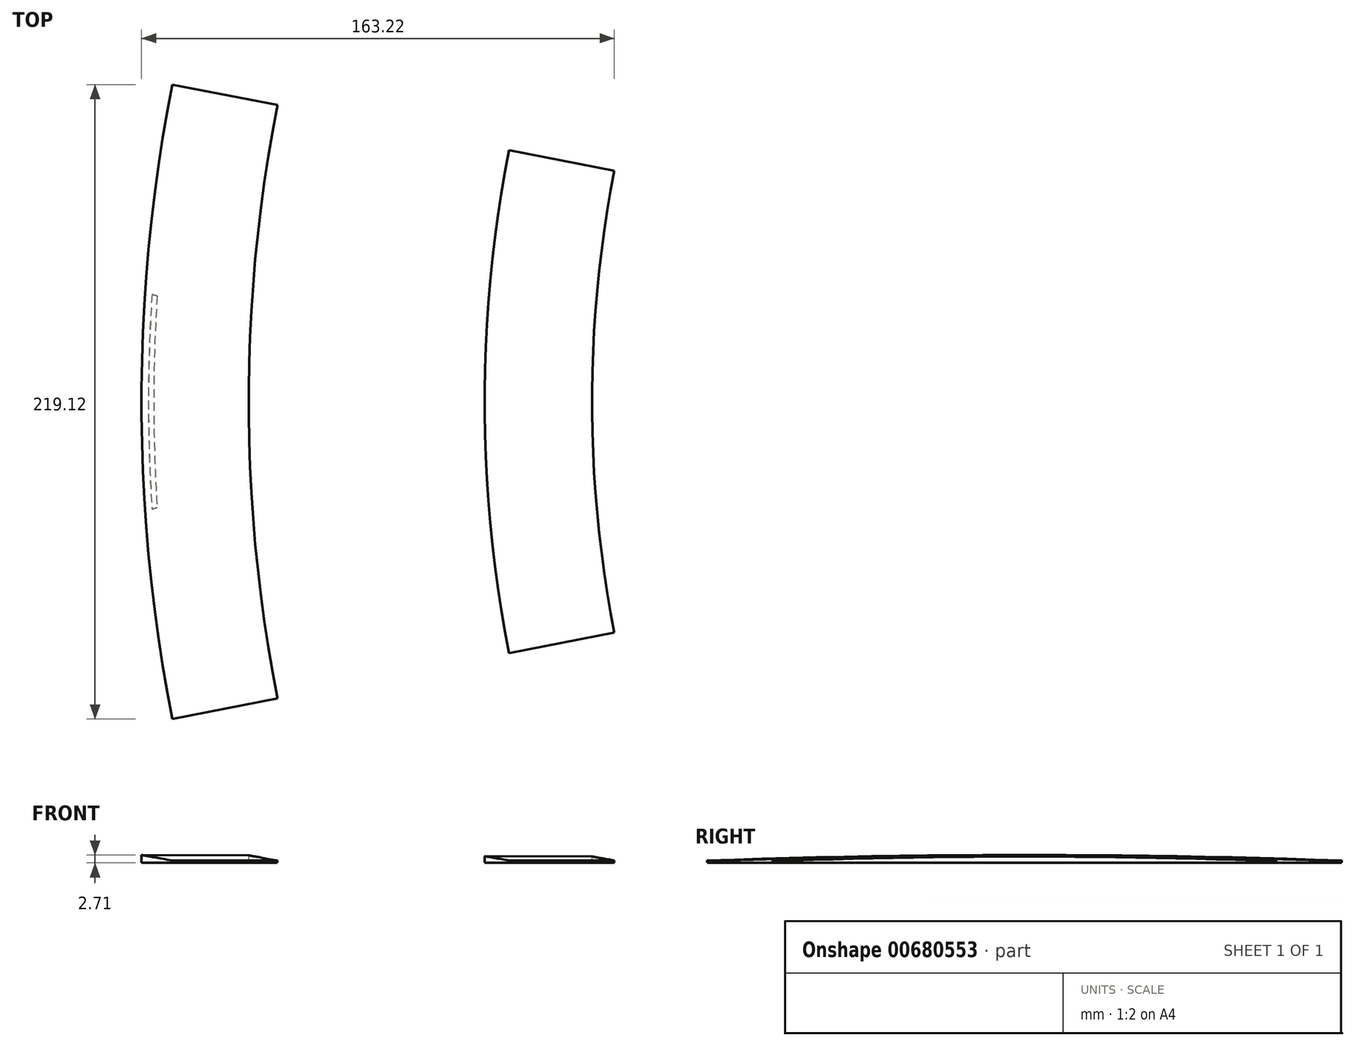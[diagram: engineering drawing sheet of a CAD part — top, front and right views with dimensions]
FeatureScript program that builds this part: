
annotation { "Feature Type Name" : "Feature", "Feature Type Description" : "" }
export const myFeature = defineFeature(function(context is Context, id is Id, definition is map)
    precondition{}
    {
        {
            var Q0;
            Q0=qCreatedBy(makeId("Front.planeOp"),FACE);
            var sketch = newSketch(context, id + "F0", { "sketchPlane" : qUnion([Q0])});
            skLineSegment(sketch, "E0", {"start": v(0, 1.91) * mm, "end": v(570.67, 0) * mm});
            skLineSegment(sketch, "E1", {"start": v(570.67, 0) * mm, "end": v(553.13, -97.53) * mm});
            skLineSegment(sketch, "E2", {"start": v(553.13, -97.53) * mm, "end": v(0, 1.91) * mm});
            skLineSegment(sketch, "E3", {"start": v(0, 1.91) * mm, "end": v(0.03, 9.71) * mm});
            skLineSegment(sketch, "E4", {"start": v(0.03, 9.71) * mm, "end": v(156.03, 9.19) * mm});
            skLineSegment(sketch, "E5", {"start": v(156.03, 9.19) * mm, "end": v(156, 1.39) * mm});
            skLineSegment(sketch, "E6", {"start": v(156, 1.39) * mm, "end": v(155.97, -7.61) * mm});
            skLineSegment(sketch, "E7", {"start": v(155.97, -7.61) * mm, "end": v(-0.03, -7.09) * mm});
            skLineSegment(sketch, "E8", {"start": v(-0.03, -7.09) * mm, "end": v(0, 1.91) * mm});
            skLineSegment(sketch, "E9", {"start": v(0.28, 9.71) * mm, "end": v(0.25, 1.91) * mm});
            skLineSegment(sketch, "E10", {"start": v(155.78, 9.2) * mm, "end": v(155.75, 1.4) * mm});
            skSolve(sketch);
        }
        {
            var Q0;
            {var subQ0=sQuery(id+"F0.wireOp",EDGE,"E9");Q0=makeQuery(id+"F0.imprint","IMPRINT",FACE,{"disambiguationData":[TD([[makeQuery(id+"F0.imprint","IMPRINT",EDGE,{"derivedFrom":subQ0}),1.0]])]});}
            var Q1;
            Q1=sQuery(id+"F0.wireOp",EDGE,"E1");
            revolve(context, id + "F1", {"entities" : qUnion([Q0]), "axis" : qUnion([Q1]), "revolveType" : RevolveType.SYMMETRIC, "angle" : 22.44 * degree});
        }
        {
            var Q0;
            Q0=qCreatedBy(makeId("Front.planeOp"),FACE);
            var sketch = newSketch(context, id + "F2", { "sketchPlane" : qUnion([Q0])});
            skLineSegment(sketch, "E11.bottom", {"start": v(-24.5, 7) * mm, "end": v(187.03, 7) * mm});
            skLineSegment(sketch, "E11.top", {"start": v(-24.5, -14.67) * mm, "end": v(187.03, -14.67) * mm});
            skLineSegment(sketch, "E11.left", {"start": v(-24.5, 7) * mm, "end": v(-24.5, -14.67) * mm});
            skLineSegment(sketch, "E11.right", {"start": v(187.03, 7) * mm, "end": v(187.03, -14.67) * mm});
            skSolve(sketch);
        }
        {
            var Q0;
            Q0=makeQuery(id+"F2.imprint","IMPRINT",FACE,{"disambiguationData":[TD([[makeQuery(id+"F2.imprint","IMPRINT",EDGE,{"derivedFrom":sQuery(id+"F2.wireOp",EDGE,"E11.bottom")}),-1.0]])]});
            extrude(context, id + "F3", {"entities" : qUnion([Q0]), "operationType" : NewBodyOperationType.REMOVE, "endBound" : BoundingType.SYMMETRIC, "depth" : 272.4 * mm, "offsetDistance" : 25 * mm});
        }
        {
            var Q0;
            Q0=qCreatedBy(makeId("Front.planeOp"),FACE);
            var sketch = newSketch(context, id + "F4", { "sketchPlane" : qUnion([Q0])});
            skLineSegment(sketch, "E12", {"start": v(0, 1.91) * mm, "end": v(570.67, 0) * mm});
            skLineSegment(sketch, "E13", {"start": v(570.67, 0) * mm, "end": v(553.13, -97.53) * mm});
            skLineSegment(sketch, "E14", {"start": v(553.13, -97.53) * mm, "end": v(0, 1.91) * mm});
            skLineSegment(sketch, "E15", {"start": v(0, 1.91) * mm, "end": v(0, 2.71) * mm});
            skLineSegment(sketch, "E16", {"start": v(0, 2.71) * mm, "end": v(1.7, 2.71) * mm});
            skLineSegment(sketch, "E17", {"start": v(1.7, 2.71) * mm, "end": v(2.7, 7.22) * mm});
            skLineSegment(sketch, "E18", {"start": v(2.7, 7.22) * mm, "end": v(4.5, 7.21) * mm});
            skLineSegment(sketch, "E19", {"start": v(4.5, 7.21) * mm, "end": v(4.49, 2.71) * mm});
            skLineSegment(sketch, "E20", {"start": v(4.49, 2.71) * mm, "end": v(1.7, 2.71) * mm});
            skLineSegment(sketch, "E21", {"start": v(156, 1.39) * mm, "end": v(156, 2.19) * mm});
            skLineSegment(sketch, "E22", {"start": v(156, 2.19) * mm, "end": v(154.3, 2.19) * mm});
            skLineSegment(sketch, "E23", {"start": v(154.3, 2.19) * mm, "end": v(153.3, 6.69) * mm});
            skLineSegment(sketch, "E24", {"start": v(153.3, 6.69) * mm, "end": v(151.5, 6.7) * mm});
            skLineSegment(sketch, "E25", {"start": v(151.5, 6.7) * mm, "end": v(151.49, 2.19) * mm});
            skLineSegment(sketch, "E26", {"start": v(151.49, 2.19) * mm, "end": v(154.3, 2.19) * mm});
            skLineSegment(sketch, "E27", {"start": v(37.29, 15.7) * mm, "end": v(37.25, 4.66) * mm});
            skLineSegment(sketch, "E28", {"start": v(37.25, 4.66) * mm, "end": v(40.75, 4.66) * mm});
            skLineSegment(sketch, "E29", {"start": v(40.75, 4.66) * mm, "end": v(40.8, 17.47) * mm});
            skLineSegment(sketch, "E30", {"start": v(40.8, 17.47) * mm, "end": v(37.29, 15.7) * mm});
            skLineSegment(sketch, "E31", {"start": v(115.3, 19.83) * mm, "end": v(115.25, 3.55) * mm});
            skLineSegment(sketch, "E32", {"start": v(115.25, 3.55) * mm, "end": v(118.75, 3.4) * mm});
            skLineSegment(sketch, "E33", {"start": v(118.75, 3.4) * mm, "end": v(118.8, 20.02) * mm});
            skLineSegment(sketch, "E34", {"start": v(118.8, 20.02) * mm, "end": v(115.3, 19.83) * mm});
            skLineSegment(sketch, "E35", {"start": v(40.8, 17.47) * mm, "end": v(115.3, 19.83) * mm});
            skLineSegment(sketch, "E36", {"start": v(40.75, 4.66) * mm, "end": v(115.25, 3.55) * mm});
            skSolve(sketch);
        }
        {
            var Q0;
            Q0=makeQuery(id+"F4.imprint","IMPRINT",FACE,{"disambiguationData":[TD([[makeQuery(id+"F4.imprint","IMPRINT",EDGE,{"derivedFrom":sQuery(id+"F4.wireOp",EDGE,"E17")}),-1.0]])]});
            var Q1;
            Q1=makeQuery(id+"F4.imprint","IMPRINT",FACE,{"disambiguationData":[TD([[makeQuery(id+"F4.imprint","IMPRINT",EDGE,{"derivedFrom":sQuery(id+"F4.wireOp",EDGE,"E23")}),1.0]])]});
            var Q2;
            Q2=makeQuery(id+"F4.imprint","IMPRINT",FACE,{"disambiguationData":[TD([[makeQuery(id+"F4.imprint","IMPRINT",EDGE,{"derivedFrom":sQuery(id+"F4.wireOp",EDGE,"E27")}),1.0]])]});
            var Q3;
            Q3=makeQuery(id+"F4.imprint","IMPRINT",FACE,{"disambiguationData":[TD([[makeQuery(id+"F4.imprint","IMPRINT",EDGE,{"derivedFrom":sQuery(id+"F4.wireOp",EDGE,"E31")}),1.0]])]});
            var Q4;
            Q4=makeQuery(id+"F4.imprint","IMPRINT",FACE,{"disambiguationData":[TD([[makeQuery(id+"F4.imprint","IMPRINT",EDGE,{"derivedFrom":sQuery(id+"F4.wireOp",EDGE,"E29")}),-1.0]])]});
            var Q5;
            Q5=sQuery(id+"F4.wireOp",EDGE,"E13");
            revolve(context, id + "F5", {"operationType" : NewBodyOperationType.REMOVE, "entities" : qUnion([Q0, Q1, Q2, Q3, Q4]), "axis" : qUnion([Q5]), "revolveType" : RevolveType.SYMMETRIC, "angle" : 30 * degree});
        }
    });
